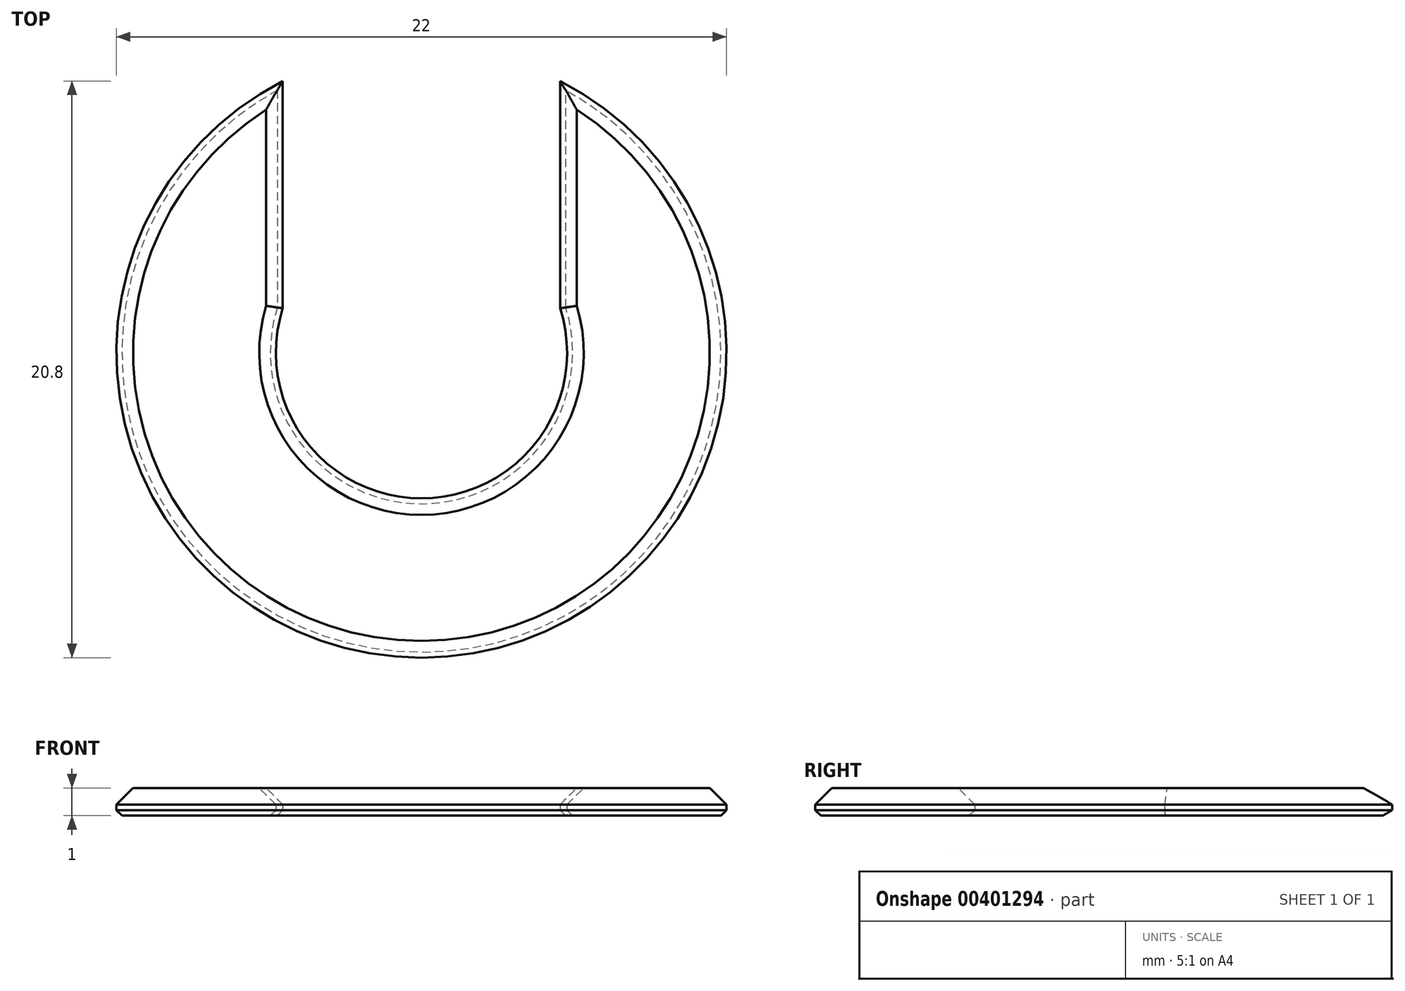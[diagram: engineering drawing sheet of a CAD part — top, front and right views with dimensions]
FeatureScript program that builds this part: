
annotation { "Feature Type Name" : "Feature", "Feature Type Description" : "" }
export const myFeature = defineFeature(function(context is Context, id is Id, definition is map)
    precondition{}
    {
        {
            var Q0;
            Q0=qCreatedBy(makeId("Top.planeOp"),FACE);
            var sketch = newSketch(context, id + "F0", { "sketchPlane" : qUnion([Q0])});
            skCircle(sketch, "E0", {"center": v(0, 0) * mm, "radius": 5.25 * mm});
            skCircle(sketch, "E1", {"center": v(0, 0) * mm, "radius": 11 * mm});
            skLineSegment(sketch, "E2.bottom", {"start": v(-5, 0) * mm, "end": v(5, 0) * mm});
            skLineSegment(sketch, "E2.top", {"start": v(-5, 13.66) * mm, "end": v(5, 13.66) * mm});
            skLineSegment(sketch, "E2.left", {"start": v(-5, 0) * mm, "end": v(-5, 13.66) * mm});
            skLineSegment(sketch, "E2.right", {"start": v(5, 0) * mm, "end": v(5, 13.66) * mm});
            skSolve(sketch);
        }
        {
            var Q0;
            {var subQ0=sQuery(id+"F0.wireOp",EDGE,"E2.left");var subQ1=sQuery(id+"F0.wireOp",EDGE,"E0");var subQ2=makeQuery(id+"F0.imprint","INTERSECT",VERTEX,{"derivedFrom":[subQ1,subQ0]});Q0=makeQuery(id+"F0.imprint","IMPRINT",FACE,{"disambiguationData":[TD([[makeQuery(id+"F0.imprint","IMPRINT",EDGE,{"disambiguationData":[TD([[subQ2,-1.0]])],"derivedFrom":subQ1}),-1.0]])]});}
            extrude(context, id + "F1", {"entities" : qUnion([Q0]), "depth" : 1 * mm});
        }
        {
            var Q0;
            Q0=makeQuery(id+"F1.opExtrude","CAP_FACE",FACE,{"disambiguationData":[OSD([sQuery(id+"F0.wireOp",EDGE,"E0"),sQuery(id+"F0.wireOp",EDGE,"E1"),sQuery(id+"F0.wireOp",EDGE,"E2.left"),sQuery(id+"F0.wireOp",EDGE,"E2.right")])],"isStart":true});
            chamfer(context, id + "F2", {"entities" : qUnion([Q0]), "width" : .2 * mm, "tangentPropagation" : true});
        }
        {
            var Q0;
            Q0=makeQuery(id+"F1.opExtrude","CAP_FACE",FACE,{"disambiguationData":[OSD([sQuery(id+"F0.wireOp",EDGE,"E0"),sQuery(id+"F0.wireOp",EDGE,"E1"),sQuery(id+"F0.wireOp",EDGE,"E2.left"),sQuery(id+"F0.wireOp",EDGE,"E2.right")])],"isStart":false});
            chamfer(context, id + "F3", {"entities" : qUnion([Q0]), "width" : .6 * mm, "tangentPropagation" : true});
        }
    });
